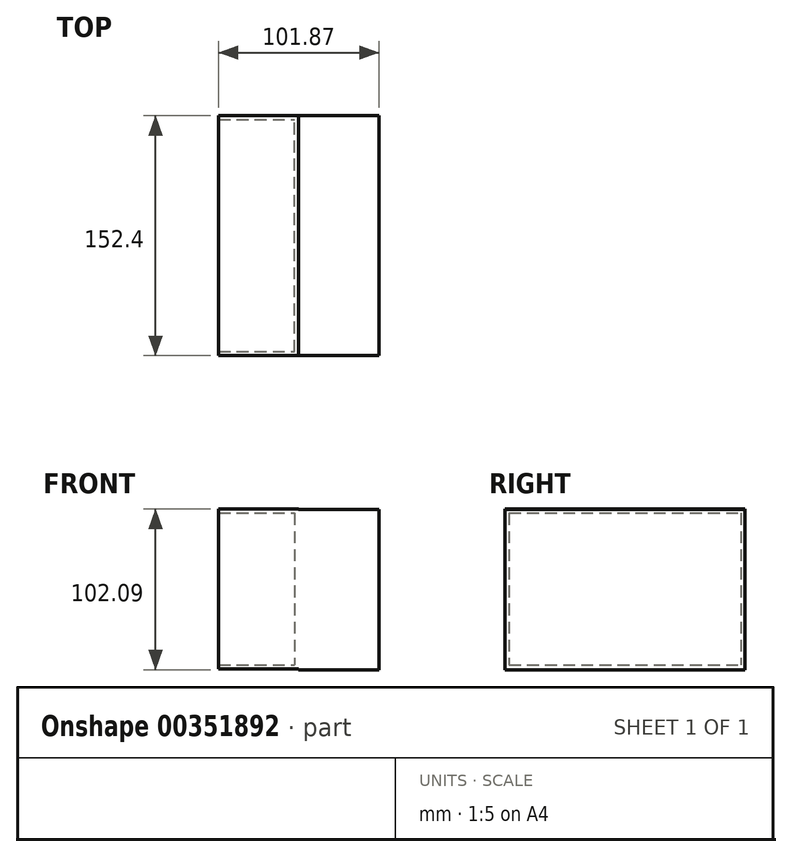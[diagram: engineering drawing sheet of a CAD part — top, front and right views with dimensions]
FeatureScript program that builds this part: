
annotation { "Feature Type Name" : "Feature", "Feature Type Description" : "" }
export const myFeature = defineFeature(function(context is Context, id is Id, definition is map)
    precondition{}
    {
        {
            var Q0;
            Q0=qCreatedBy(makeId("Front.planeOp"),FACE);
            var sketch = newSketch(context, id + "F0", { "sketchPlane" : qUnion([Q0])});
            skLineSegment(sketch, "E0.bottom", {"start": v(-50.8, 56.13) * mm, "end": v(0, 56.13) * mm});
            skLineSegment(sketch, "E0.top", {"start": v(-50.8, -45.47) * mm, "end": v(0, -45.47) * mm});
            skLineSegment(sketch, "E0.left", {"start": v(-50.8, 56.13) * mm, "end": v(-50.8, -45.47) * mm});
            skLineSegment(sketch, "E0.right", {"start": v(0, 56.13) * mm, "end": v(0, -45.47) * mm});
            skSolve(sketch);
        }
        {
            var Q0;
            Q0 = qSketchRegion(id + "F0", true);
            extrude(context, id + "F1", {"entities" : qUnion([Q0]), "depth" : 152.4 * mm});
        }
        {
            var Q0;
            Q0=makeQuery(id+"F1.opExtrude","SWEPT_FACE",FACE,{"disambiguationData":[OSD([sQuery(id+"F0.wireOp",EDGE,"E0.left")])]});
            shell(context, id + "F2", {"entities" : qUnion([Q0]), "thickness" : 2.54 * mm});
        }
        {
            var Q0;
            Q0=qCreatedBy(makeId("Front.planeOp"),FACE);
            var sketch = newSketch(context, id + "F3", { "sketchPlane" : qUnion([Q0])});
            skLineSegment(sketch, "E1", {"start": v(0, 55.87) * mm, "end": v(51.07, 55.87) * mm});
            skLineSegment(sketch, "E2", {"start": v(51.07, 55.87) * mm, "end": v(51.07, -45.96) * mm});
            skLineSegment(sketch, "E3", {"start": v(51.07, -45.96) * mm, "end": v(0, -45.96) * mm});
            skLineSegment(sketch, "E4", {"start": v(0, -45.96) * mm, "end": v(0, 55.87) * mm});
            skSolve(sketch);
        }
        {
            var Q0;
            Q0 = qSketchRegion(id + "F3", true);
            extrude(context, id + "F4", {"entities" : qUnion([Q0]), "operationType" : NewBodyOperationType.ADD, "depth" : 152.4 * mm});
        }
    });
